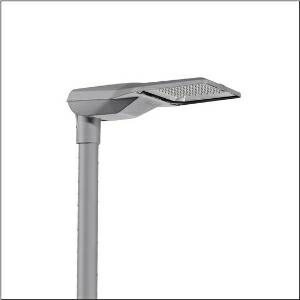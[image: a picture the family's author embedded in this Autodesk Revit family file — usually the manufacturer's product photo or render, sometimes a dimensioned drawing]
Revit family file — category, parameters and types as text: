
# Revit family: streetlight_sl_21_iq_midi___stw1_0a_5xe3e61g08nb_0b2e
name_source: partatom
category: Lighting Fixtures
units: mm (PartAtom-declared; Revit-internal decimal feet)

## family parameters
Cut with Voids When Loaded = No
Host = Face
Light Source = No
Part Type = Normal
Room Calculation Point = No
Round Connector Dimension = Use Diameter
Shared = No

## types (1)
- --- (1 x LED, 20820 lm, 155.5 W, 2700K)
    Apparent Load = 155 VA
    CIE Flux Codes = 39 75 98 100 100
    Color Rendering = 70
    Color Temperature = 2700K
    Default Elevation = 1800 mm
    Description = Streetlight SL 21 iQ midi, mast luminaire, primary light control with lens, of PMMA, primary optical cover: cover, of toughened safety glass, transparent, light distribution: STW1.0a, light emission: direct distribution, primary light characteristic: asymmetric, installation type: post-top, side-entry, LED, High Power LED, rated luminous flux: 20.820lm, luminous efficacy: 134lm/W, light colour: 727, colour temperature: 2700K, control gear: iQ Street-Remote, control: Street-Remote, Auto-Match, Temp-Guard, Lumen-Switch, Night-Set, Smart-Wire, Light-Fading, Desk-Remote (wireless, voltage-free reading and setting of iQ features in the workshop via application-optimized NFC function/RFID function), optimised constant luminous flux control (CLO 2.0), pre-setting: linear dimming characteristic, mains connection: 230..240V, AC, 50/60Hz, start of lifetime: 156W, end of service life: 162W, reduction: 69W, luminaire housing, of diecast aluminium, powder-coated, SITECO metallic grey (DB 702S), corrosivity category C5 high according to DIN EN ISO 12944, please order mast flange separately, inclination adjustable: 0°, 5°, 10°, 15°, sealing non-destructively replaceable, multi-level sealing system, length: 644mm, width: 335mm, height: 110mm, mast flange for spigot size: 42mm (side-entry): 5XC10008XM4, 60/48mm (side-entry/post-top): 5XC10108XM2, 76/60mm (side-entry/post-top): 5XC10108XM1, mounting height: 4..8m, protection rating (complete): IP66, insulation class (complete): insulation class II (safety insulation), certification: CE, ENEC, ENEC+, VDE, impact resistance: IK10, permissible operating ambient temperature for outdoor applications: -40..+50°C, standard-compliant lighting for roads and squares, packaging unit: 1 piece

Light Distribution: STW1.0a
    Height = 111 mm
    Lamp = 1 x LED
    Lamp Light Flux = 20820 lm
    Lamp Power = 155.5 W
    Lamp count = 1
    Length = 644 mm
    Luminous efficacy = 134 lm/W
    Manufacturer = Siteco
    ModVariant = No
    Model = 5XE3E61G08NB
    Number of Poles = 1
    OnlyDefault = Yes
    Power Factor = 1
    Product Name = Streetlight SL 21 iQ midi | STW1.0a
    Product group = mast luminaire | pylon top
    ProductGroupID = 6100
    Protection Class = Protection class II
    Protection Degree = IP 66
    RLX_Detail_Level = 1
    RLX_Emergency_Light_Flux = 0 lm
    RLX_Emergency_Type = 0
    RLX_Emergency_Type_DB = No
    RlxData = <blob elided: 27229 chars, md5=ab07bd66>
    Socket = socket
    Standby Power = 0 W
    System Light Flux = 20820 lm
    System Power = 155 W
    Type Comments = factory setting: luminous flux: 100 % | dim-lin: 254 | 823 mA
    Type Image = l_1004298.jpg
    URL = http://relux.com
    VarID = @adj_169201
    Voltage = 0 V
    Weight = 0.00 kg
    Width = 336 mm

## geometry (parser evidence)
native form markers: Blend x4, Sweep x10
no freeform markers — native parametric forms only
